# Revit family: Haworth_XSeries_Locker_Cubby9Doors
name_source: partatom
category: Furniture Systems
units: mm (PartAtom-declared; Revit-internal decimal feet)

## family parameters
Always vertical = Yes
Cut with Voids When Loaded = No
OmniClass Number = 23.40.70.14.64.21
OmniClass Title = Systems Furniture
Part Type = Normal
Room Calculation Point = No
Round Connector Dimension = Use Diameter
Shared = No
Work Plane-Based = No

## types (1)
- 18d 36w 63h
    Actual Depth = 18 3/4"
    Actual Height = 63 1/2"
    Actual Width = 36"
    Assembly Code = E2020200
    Base Height = 1 7/8"
    Classic Pull = No
    Crescent Pull = No
    Custom Depth = No
    Custom Height = No
    Custom Size = No
    Custom Width = No
    Depth = 18 3/4"
    Description = Haworth XSeries Locker - Cubby 9 Doors - 18d 36w 63h
    Door Gap = 1/8"
    Door Height = 20"
    Door Offset = 1/16"
    Door Width = 11 13/16"
    Height = 63 1/2"
    J Pull = No
    Linear Pull = Yes
    Manufacturer = Haworth
    Max. Depth = 18 3/4"
    Max. Height = 63 1/2"
    Max. Width = 36"
    Min. Depth = 18 3/4"
    Min. Height = 63 1/2"
    Min. Width = 36"
    Model = JA18-6336
    Panel Thickness = 3/4"
    Panel Thickness Half = 3/8"
    Pull Ellipse = No
    Pull Finish = Haworth _ Metal _ Brushed Aluminum
    Pull Height = 10"
    Pull Offset Centerline = 10 1/2"
    Radius Pull = No
    Revision Number = 3
    Size = Verify Final Dim. w/ Haworth
    Standard Depths = 18.75 in.
    Standard Heights = 63.5 in.
    Standard Widths = 36 in.
    Sustainability Info = https://www.haworth.com
    Taper Pull = No
    Top Height = 1 1/4"
    URL = http://www.haworth.com
    URL - Product = https://www.haworth.com
    Warranty = https://cdn.shopify.com
    Width = 36"

## geometry (parser evidence)
native form markers: Sweep x7
no freeform markers — native parametric forms only
